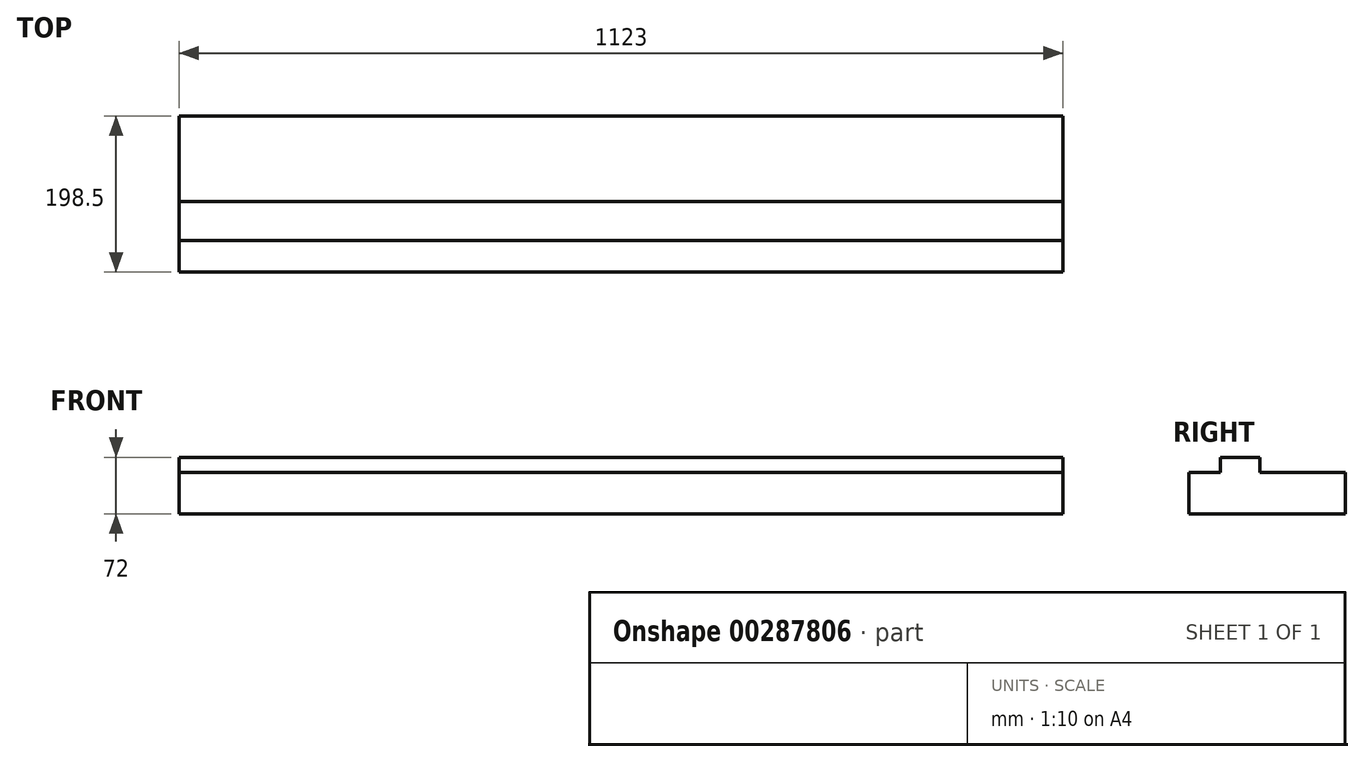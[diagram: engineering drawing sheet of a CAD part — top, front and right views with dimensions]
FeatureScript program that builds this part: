
annotation { "Feature Type Name" : "Feature", "Feature Type Description" : "" }
export const myFeature = defineFeature(function(context is Context, id is Id, definition is map)
    precondition{}
    {
        {
            var Q0;
            Q0=qCreatedBy(makeId("Right.planeOp"),FACE);
            var sketch = newSketch(context, id + "F0", { "sketchPlane" : qUnion([Q0])});
            skLineSegment(sketch, "E0.bottom", {"start": v(0, 0) * mm, "end": v(198.5, 0) * mm});
            skLineSegment(sketch, "E0.top", {"start": v(40, 72) * mm, "end": v(90, 72) * mm});
            skLineSegment(sketch, "E0.left", {"start": v(0, 0) * mm, "end": v(0, 52.5) * mm});
            skLineSegment(sketch, "E1", {"start": v(0, 52.5) * mm, "end": v(40, 52.5) * mm});
            skLineSegment(sketch, "E2", {"start": v(40, 52.5) * mm, "end": v(40, 72) * mm});
            skLineSegment(sketch, "E3", {"start": v(198.5, 52.5) * mm, "end": v(198.5, 0) * mm});
            skLineSegment(sketch, "E4", {"start": v(90, 72) * mm, "end": v(90, 52.5) * mm});
            skLineSegment(sketch, "E5", {"start": v(90, 52.5) * mm, "end": v(198.5, 52.5) * mm});
            skSolve(sketch);
        }
        {
            var Q0;
            Q0=makeQuery(id+"F0.imprint","IMPRINT",FACE,{"disambiguationData":[TD([[makeQuery(id+"F0.imprint","IMPRINT",EDGE,{"derivedFrom":sQuery(id+"F0.wireOp",EDGE,"E0.bottom")}),1.0]])]});
            extrude(context, id + "F1", {"entities" : qUnion([Q0]), "endBound" : BoundingType.SYMMETRIC, "depth" : 1123 * mm});
        }
    });
